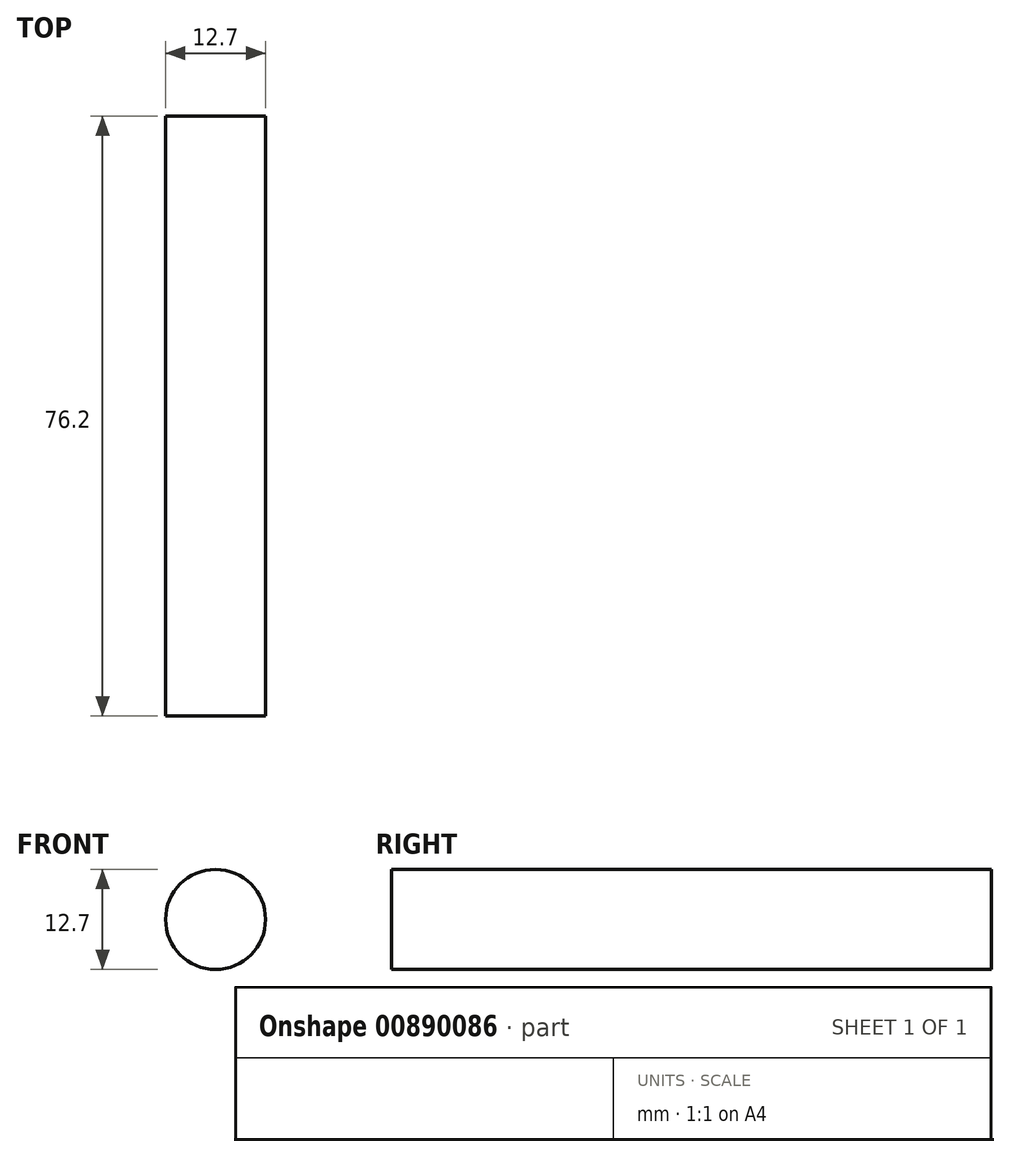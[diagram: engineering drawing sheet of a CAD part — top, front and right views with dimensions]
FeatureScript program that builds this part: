
annotation { "Feature Type Name" : "Feature", "Feature Type Description" : "" }
export const myFeature = defineFeature(function(context is Context, id is Id, definition is map)
    precondition{}
    {
        {
            var Q0;
            Q0=qCreatedBy(makeId("Front.planeOp"),FACE);
            var sketch = newSketch(context, id + "F0", { "sketchPlane" : qUnion([Q0])});
            skCircle(sketch, "E0", {"center": v(0, 0) * mm, "radius": 6.35 * mm});
            skSolve(sketch);
        }
        {
            var Q0;
            Q0 = qSketchRegion(id + "F0", true);
            extrude(context, id + "F1", {"entities" : qUnion([Q0]), "depth" : 76.2 * mm, "offsetDistance" : 25.4 * mm});
        }
    });
